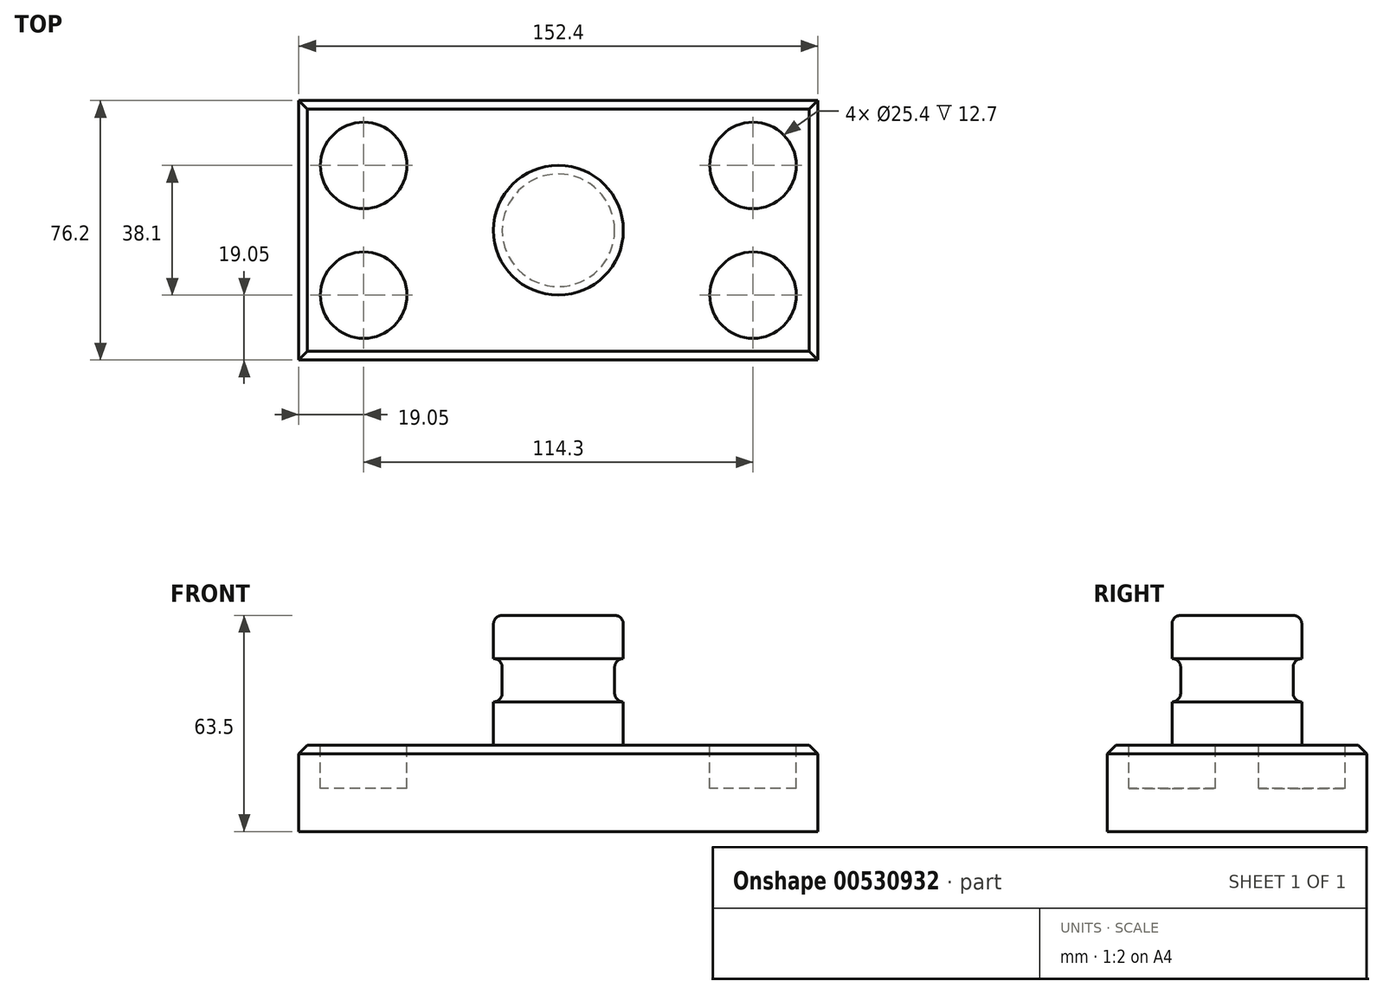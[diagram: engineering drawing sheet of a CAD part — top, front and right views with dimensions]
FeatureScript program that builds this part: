
annotation { "Feature Type Name" : "Feature", "Feature Type Description" : "" }
export const myFeature = defineFeature(function(context is Context, id is Id, definition is map)
    precondition{}
    {
        {
            var Q0;
            Q0=qCreatedBy(makeId("Top.planeOp"),FACE);
            var sketch = newSketch(context, id + "F0", { "sketchPlane" : qUnion([Q0])});
            skLineSegment(sketch, "E0.bottom", {"start": v(76.2, 38.1) * mm, "end": v(-76.2, 38.1) * mm});
            skLineSegment(sketch, "E0.top", {"start": v(76.2, -38.1) * mm, "end": v(-76.2, -38.1) * mm});
            skLineSegment(sketch, "E0.left", {"start": v(76.2, 38.1) * mm, "end": v(76.2, -38.1) * mm});
            skLineSegment(sketch, "E0.right", {"start": v(-76.2, 38.1) * mm, "end": v(-76.2, -38.1) * mm});
            skPoint(sketch, "E0.middle", {"position": v(0, 0) * mm});
            skSolve(sketch);
        }
        {
            var Q0;
            Q0=makeQuery(id+"F0.imprint","IMPRINT",FACE,{"disambiguationData":[TD([[makeQuery(id+"F0.imprint","IMPRINT",EDGE,{"derivedFrom":sQuery(id+"F0.wireOp",EDGE,"E0.bottom")}),1.0]])]});
            extrude(context, id + "F1", {"entities" : qUnion([Q0]), "depth" : 25.4 * mm, "offsetDistance" : 25.4 * mm});
        }
        {
            var Q0;
            Q0=makeQuery(id+"F1.opExtrude","CAP_FACE",FACE,{"disambiguationData":[OSD([sQuery(id+"F0.wireOp",EDGE,"E0.bottom"),sQuery(id+"F0.wireOp",EDGE,"E0.top"),sQuery(id+"F0.wireOp",EDGE,"E0.left"),sQuery(id+"F0.wireOp",EDGE,"E0.right")])],"isStart":false});
            var sketch = newSketch(context, id + "F2", { "sketchPlane" : qUnion([Q0])});
            skCircle(sketch, "E1", {"center": v(57.15, -19.05) * mm, "radius": 12.7 * mm});
            skCircle(sketch, "E2", {"center": v(57.15, 19.05) * mm, "radius": 12.7 * mm});
            skCircle(sketch, "E3", {"center": v(-57.15, 19.05) * mm, "radius": 12.7 * mm});
            skCircle(sketch, "E4", {"center": v(-57.15, -19.05) * mm, "radius": 12.7 * mm});
            skSolve(sketch);
        }
        {
            var Q0;
            Q0=makeQuery(id+"F2.imprint","IMPRINT",FACE,{"disambiguationData":[TD([[makeQuery(id+"F2.imprint","IMPRINT",EDGE,{"derivedFrom":sQuery(id+"F2.wireOp",EDGE,"E1")}),1.0]])]});
            var Q1;
            Q1=makeQuery(id+"F2.imprint","IMPRINT",FACE,{"disambiguationData":[TD([[makeQuery(id+"F2.imprint","IMPRINT",EDGE,{"derivedFrom":sQuery(id+"F2.wireOp",EDGE,"E4")}),1.0]])]});
            var Q2;
            Q2=makeQuery(id+"F2.imprint","IMPRINT",FACE,{"disambiguationData":[TD([[makeQuery(id+"F2.imprint","IMPRINT",EDGE,{"derivedFrom":sQuery(id+"F2.wireOp",EDGE,"E3")}),1.0]])]});
            var Q3;
            Q3=makeQuery(id+"F2.imprint","IMPRINT",FACE,{"disambiguationData":[TD([[makeQuery(id+"F2.imprint","IMPRINT",EDGE,{"derivedFrom":sQuery(id+"F2.wireOp",EDGE,"E2")}),1.0]])]});
            extrude(context, id + "F3", {"entities" : qUnion([Q0, Q1, Q2, Q3]), "operationType" : NewBodyOperationType.REMOVE, "oppositeDirection" : true, "depth" : 12.7 * mm, "offsetDistance" : 25.4 * mm});
        }
        {
            var Q0;
            Q0=makeQuery(id+"F1.opExtrude","CAP_EDGE",EDGE,{"disambiguationData":[OSD([sQuery(id+"F0.wireOp",EDGE,"E0.top")])],"isStart":false});
            var Q1;
            Q1=makeQuery(id+"F1.opExtrude","CAP_EDGE",EDGE,{"disambiguationData":[OSD([sQuery(id+"F0.wireOp",EDGE,"E0.left")])],"isStart":false});
            var Q2;
            Q2=makeQuery(id+"F1.opExtrude","CAP_EDGE",EDGE,{"disambiguationData":[OSD([sQuery(id+"F0.wireOp",EDGE,"E0.bottom")])],"isStart":false});
            var Q3;
            Q3=makeQuery(id+"F1.opExtrude","CAP_EDGE",EDGE,{"disambiguationData":[OSD([sQuery(id+"F0.wireOp",EDGE,"E0.right")])],"isStart":false});
            chamfer(context, id + "F4", {"entities" : qUnion([Q0, Q1, Q2, Q3]), "width" : 2.54 * mm, "tangentPropagation" : true});
        }
        {
            var Q0;
            Q0=qCreatedBy(makeId("Front.planeOp"),FACE);
            var sketch = newSketch(context, id + "F5", { "sketchPlane" : qUnion([Q0])});
            skLineSegment(sketch, "E5.bottom", {"start": v(0, 25.4) * mm, "end": v(19.05, 25.4) * mm});
            skLineSegment(sketch, "E5.top", {"start": v(0, 63.5) * mm, "end": v(19.05, 63.5) * mm});
            skLineSegment(sketch, "E5.left", {"start": v(0, 25.4) * mm, "end": v(0, 63.5) * mm});
            skLineSegment(sketch, "E5.right", {"start": v(19.05, 25.4) * mm, "end": v(19.05, 63.5) * mm});
            skLineSegment(sketch, "E6.bottom", {"start": v(19.05, 50.8) * mm, "end": v(16.5, 50.8) * mm});
            skLineSegment(sketch, "E6.top", {"start": v(19.05, 38.1) * mm, "end": v(16.51, 38.1) * mm});
            skLineSegment(sketch, "E6.left", {"start": v(19.05, 50.8) * mm, "end": v(19.05, 38.1) * mm});
            skLineSegment(sketch, "E6.right", {"start": v(16.5, 50.8) * mm, "end": v(16.51, 38.1) * mm});
            skSolve(sketch);
        }
        {
            var Q0;
            Q0=makeQuery(id+"F5.imprint","IMPRINT",FACE,{"disambiguationData":[TD([[makeQuery(id+"F5.imprint","IMPRINT",EDGE,{"derivedFrom":sQuery(id+"F5.wireOp",EDGE,"E5.bottom")}),1.0]])]});
            var Q1;
            Q1=sQuery(id+"F5.wireOp",EDGE,"E5.left");
            revolve(context, id + "F6", {"operationType" : NewBodyOperationType.ADD, "entities" : qUnion([Q0]), "axis" : qUnion([Q1]), "revolveType" : RevolveType.FULL});
        }
        {
            var Q0;
            Q0=makeQuery(id+"F6.opRevolve","SWEPT_EDGE",EDGE,{"disambiguationData":[OSD([sQuery(id+"F5.wireOp",EDGE,"E6.top"),sQuery(id+"F5.wireOp",EDGE,"E6.right")])]});
            var Q1;
            Q1=makeQuery(id+"F6.opRevolve","SWEPT_EDGE",EDGE,{"disambiguationData":[OSD([sQuery(id+"F5.wireOp",EDGE,"E5.bottom"),sQuery(id+"F5.wireOp",EDGE,"E5.right")])]});
            var Q2;
            Q2=makeQuery(id+"F6.opRevolve","SWEPT_EDGE",EDGE,{"disambiguationData":[OSD([sQuery(id+"F5.wireOp",EDGE,"E6.bottom"),sQuery(id+"F5.wireOp",EDGE,"E6.right")])]});
            var Q3;
            Q3=makeQuery(id+"F6.opRevolve","SWEPT_EDGE",EDGE,{"disambiguationData":[OSD([sQuery(id+"F5.wireOp",EDGE,"E5.top"),sQuery(id+"F5.wireOp",EDGE,"E5.right")])]});
            fillet(context, id + "F7", {"entities" : qUnion([Q0, Q1, Q2, Q3]), "radius" : 2.54 * mm, "tangentPropagation" : true, "allowEdgeOverflow" : false});
        }
    });
